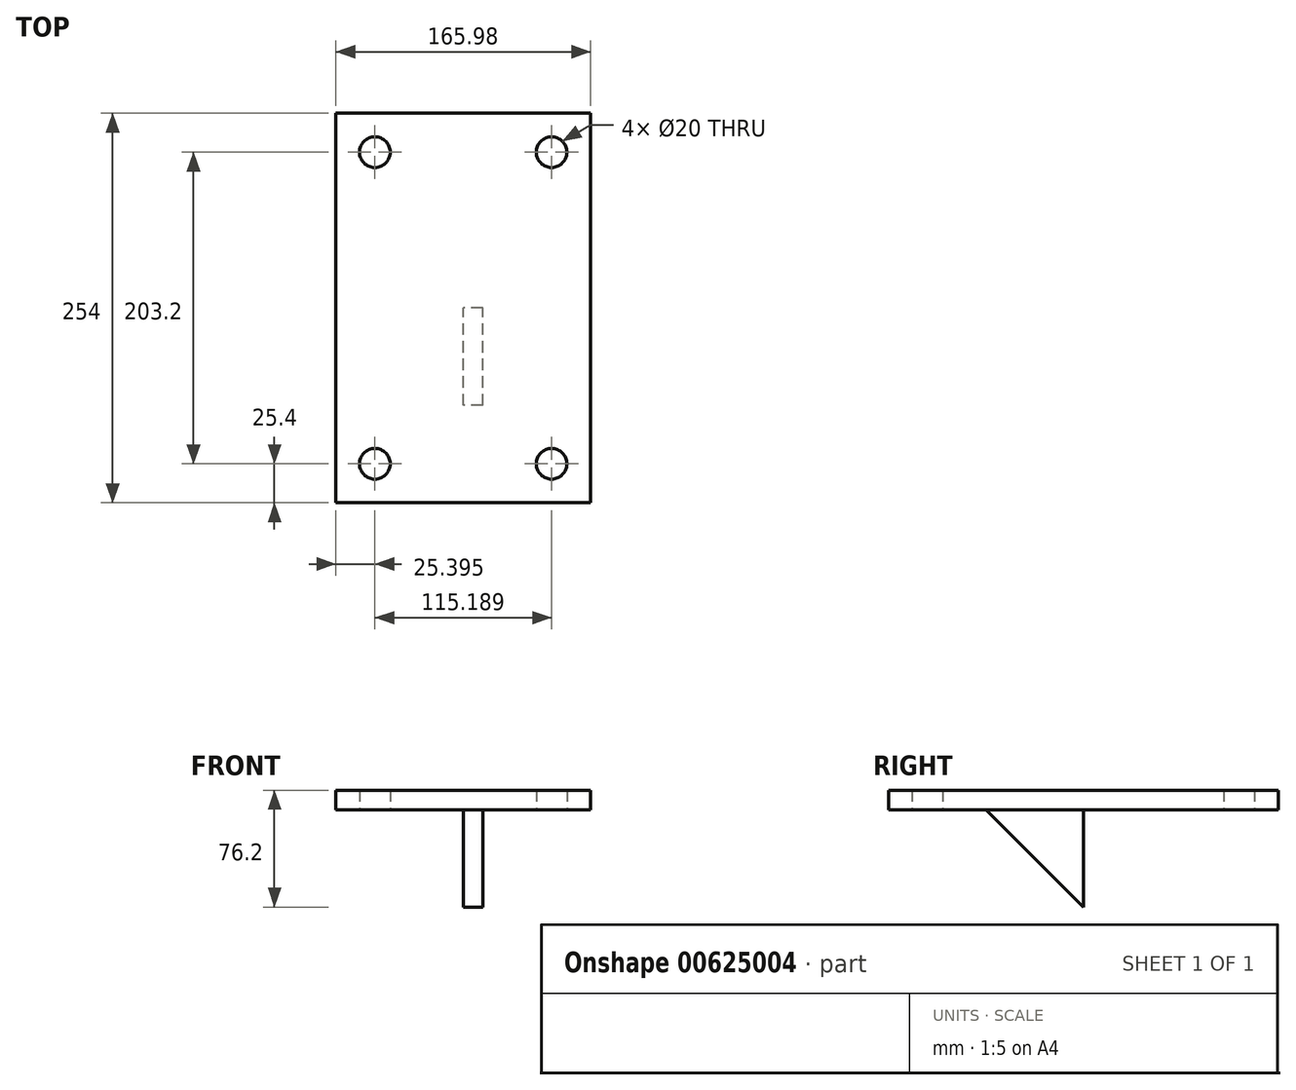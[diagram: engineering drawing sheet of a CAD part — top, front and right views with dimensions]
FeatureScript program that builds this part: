
annotation { "Feature Type Name" : "Feature", "Feature Type Description" : "" }
export const myFeature = defineFeature(function(context is Context, id is Id, definition is map)
    precondition{}
    {
        {
            var Q0;
            Q0=qCreatedBy(makeId("Top.planeOp"),FACE);
            var sketch = newSketch(context, id + "F0", { "sketchPlane" : qUnion([Q0])});
            skLineSegment(sketch, "E0.bottom", {"start": v(83, -127) * mm, "end": v(-83, -127) * mm});
            skLineSegment(sketch, "E0.top", {"start": v(83, 127) * mm, "end": v(-83, 127) * mm});
            skLineSegment(sketch, "E0.left", {"start": v(83, -127) * mm, "end": v(83, 127) * mm});
            skLineSegment(sketch, "E0.right", {"start": v(-83, -127) * mm, "end": v(-83, 127) * mm});
            skPoint(sketch, "E0.middle", {"position": v(0, 0) * mm});
            skCircle(sketch, "E1", {"center": v(-57.6, 101.6) * mm, "radius": 10 * mm});
            skCircle(sketch, "E2", {"center": v(57.6, 101.6) * mm, "radius": 10 * mm});
            skLineSegment(sketch, "E3", {"start": v(0, 127) * mm, "end": v(0, -127) * mm, "construction": true});
            skLineSegment(sketch, "E4", {"start": v(-83, 0) * mm, "end": v(83, 0) * mm, "construction": true});
            skCircle(sketch, "E5.MirrorC", {"center": v(-57.6, -101.6) * mm, "radius": 10 * mm});
            skCircle(sketch, "E6.MirrorC", {"center": v(57.6, -101.6) * mm, "radius": 10 * mm});
            skSolve(sketch);
        }
        {
            var Q0;
            Q0 = qSketchRegion(id + "F0", true);
            extrude(context, id + "F1", {"entities" : qUnion([Q0]), "depth" : 12.7 * mm, "offsetDistance" : 25.4 * mm});
        }
        {
            var Q0;
            Q0=qCreatedBy(makeId("Right.planeOp"),FACE);
            var sketch = newSketch(context, id + "F2", { "sketchPlane" : qUnion([Q0])});
            skLineSegment(sketch, "E7", {"start": v(0, 0) * mm, "end": v(0, -63.5) * mm});
            skLineSegment(sketch, "E8", {"start": v(0, -63.5) * mm, "end": v(-63.5, 0) * mm});
            skLineSegment(sketch, "E9", {"start": v(-63.5, 0) * mm, "end": v(0, 0) * mm});
            skSolve(sketch);
        }
        {
            var Q0;
            Q0 = qSketchRegion(id + "F2", true);
            extrude(context, id + "F3", {"entities" : qUnion([Q0]), "depth" : 12.7 * mm, "offsetDistance" : 25.4 * mm});
        }
    });
